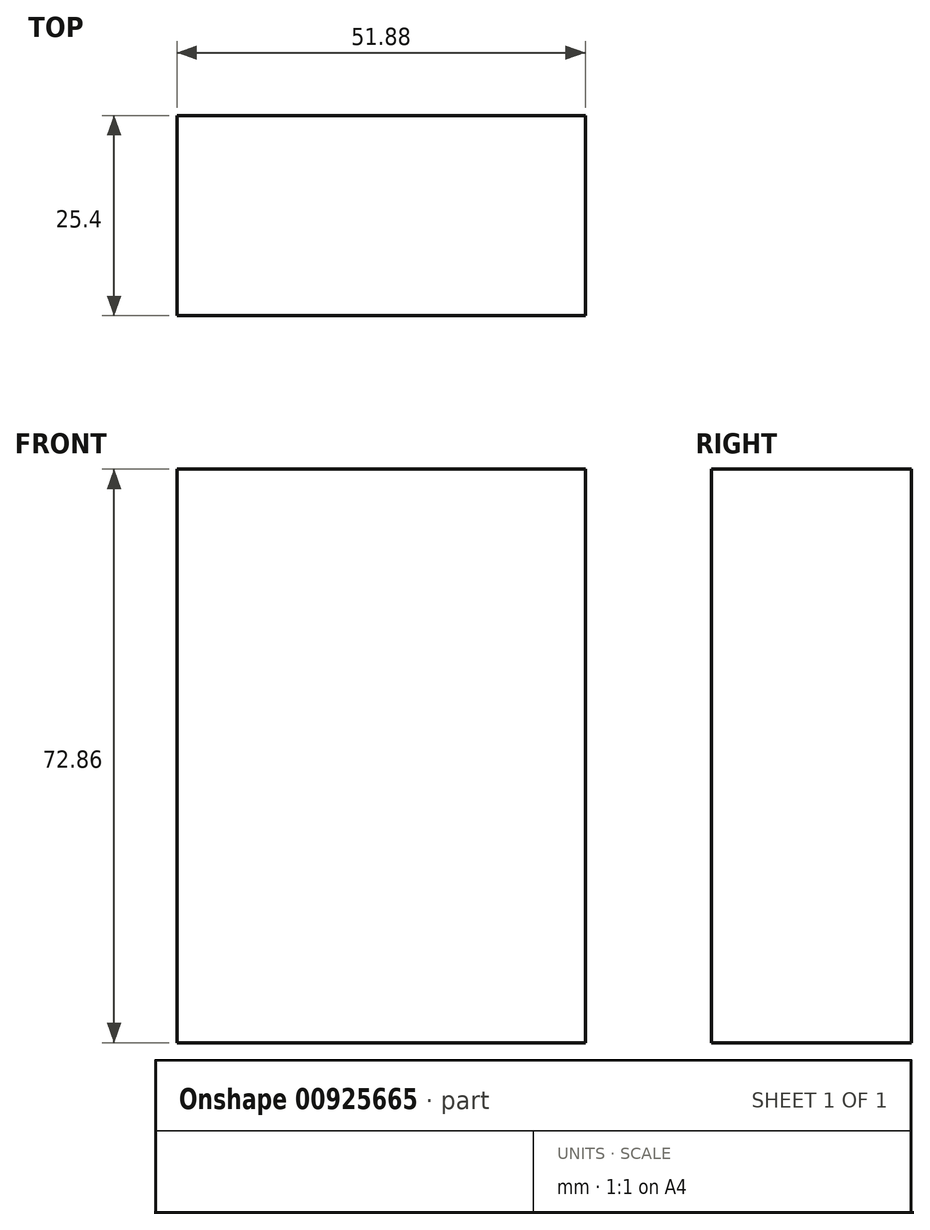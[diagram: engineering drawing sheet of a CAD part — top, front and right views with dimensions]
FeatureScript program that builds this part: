
annotation { "Feature Type Name" : "Feature", "Feature Type Description" : "" }
export const myFeature = defineFeature(function(context is Context, id is Id, definition is map)
    precondition{}
    {
        {
            var Q0;
            Q0=qCreatedBy(makeId("Front.planeOp"),FACE);
            var sketch = newSketch(context, id + "F0", { "sketchPlane" : qUnion([Q0])});
            skLineSegment(sketch, "E0.bottom", {"start": v(-104.28, 51.12) * mm, "end": v(-52.4, 51.12) * mm});
            skLineSegment(sketch, "E0.top", {"start": v(-104.28, -21.74) * mm, "end": v(-52.4, -21.74) * mm});
            skLineSegment(sketch, "E0.left", {"start": v(-104.28, 51.12) * mm, "end": v(-104.28, -21.74) * mm});
            skLineSegment(sketch, "E0.right", {"start": v(-52.4, 51.12) * mm, "end": v(-52.4, -21.74) * mm});
            skSolve(sketch);
        }
        {
            var Q0;
            Q0=makeQuery(id+"F0.imprint","IMPRINT",FACE,{"disambiguationData":[TD([[makeQuery(id+"F0.imprint","IMPRINT",EDGE,{"derivedFrom":sQuery(id+"F0.wireOp",EDGE,"E0.bottom")}),-1.0]])]});
            extrude(context, id + "F1", {"entities" : qUnion([Q0]), "depth" : 25.4 * mm, "offsetDistance" : 25.4 * mm});
        }
    });
